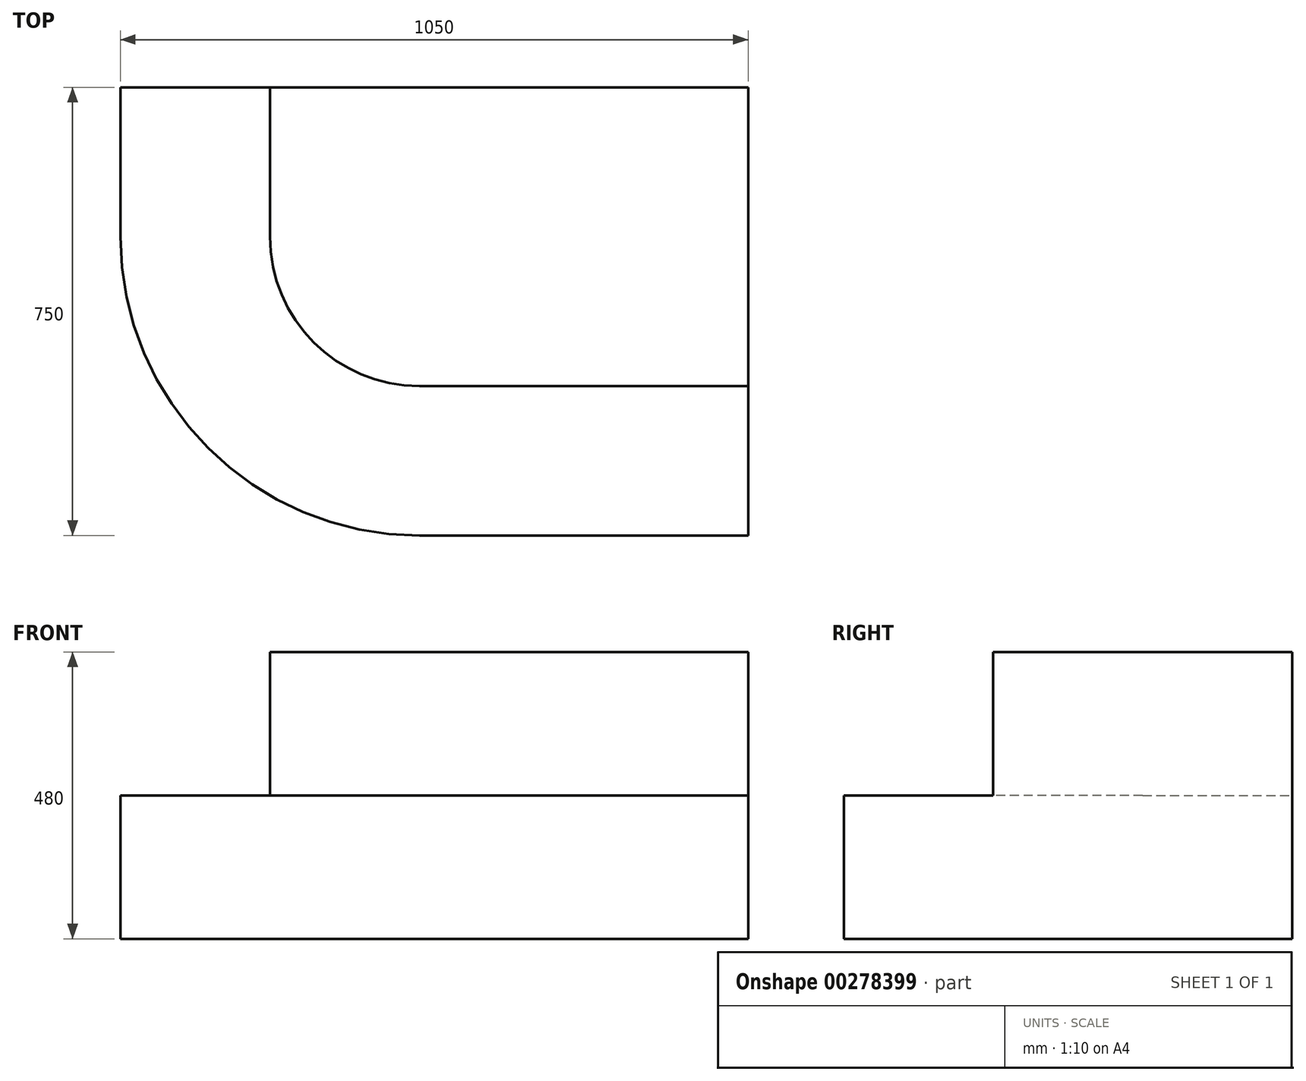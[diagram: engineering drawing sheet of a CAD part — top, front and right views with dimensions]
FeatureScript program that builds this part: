
annotation { "Feature Type Name" : "Feature", "Feature Type Description" : "" }
export const myFeature = defineFeature(function(context is Context, id is Id, definition is map)
    precondition{}
    {
        {
            var Q0;
            Q0=qCreatedBy(makeId("Top.planeOp"),FACE);
            var sketch = newSketch(context, id + "F0", { "sketchPlane" : qUnion([Q0])});
            skLineSegment(sketch, "E0", {"start": v(0, 0) * mm, "end": v(800, 0) * mm});
            skLineSegment(sketch, "E1", {"start": v(800, 0) * mm, "end": v(800, -500) * mm});
            skLineSegment(sketch, "E2", {"start": v(800, -500) * mm, "end": v(250, -500) * mm});
            skLineSegment(sketch, "E3", {"start": v(0, -250) * mm, "end": v(0, 0) * mm});
            skArc(sketch, "E4", {"start": v(0, -250) * mm, "mid": v(73.22, -426.78) * mm, "end": v(250, -500) * mm});
            skSolve(sketch);
        }
        {
            var Q0;
            Q0 = qSketchRegion(id + "F0", true);
            extrude(context, id + "F1", {"entities" : qUnion([Q0]), "oppositeDirection" : true, "depth" : 240 * mm});
        }
        {
            var Q0;
            Q0=makeQuery(id+"F1.opExtrude","CAP_FACE",FACE,{"disambiguationData":[OSD([sQuery(id+"F0.wireOp",EDGE,"E0"),sQuery(id+"F0.wireOp",EDGE,"E1"),sQuery(id+"F0.wireOp",EDGE,"E2"),sQuery(id+"F0.wireOp",EDGE,"E3"),sQuery(id+"F0.wireOp",EDGE,"E4")])],"isStart":false});
            var sketch = newSketch(context, id + "F2", { "sketchPlane" : qUnion([Q0])});
            skLineSegment(sketch, "E5.0", {"start": v(-250, 250) * mm, "end": v(-250, 0) * mm});
            skArc(sketch, "E5.1", {"start": v(-250, 250) * mm, "mid": v(-103.55, 603.55) * mm, "end": v(250, 750) * mm});
            skLineSegment(sketch, "E5.2", {"start": v(800, 750) * mm, "end": v(250, 750) * mm});
            skLineSegment(sketch, "E6", {"start": v(-250, 0) * mm, "end": v(800, 0) * mm});
            skLineSegment(sketch, "E7", {"start": v(800, 0) * mm, "end": v(800, 750) * mm});
            skSolve(sketch);
        }
        {
            var Q0;
            Q0 = qSketchRegion(id + "F2", true);
            extrude(context, id + "F3", {"entities" : qUnion([Q0]), "operationType" : NewBodyOperationType.ADD, "depth" : 240 * mm});
        }
    });
